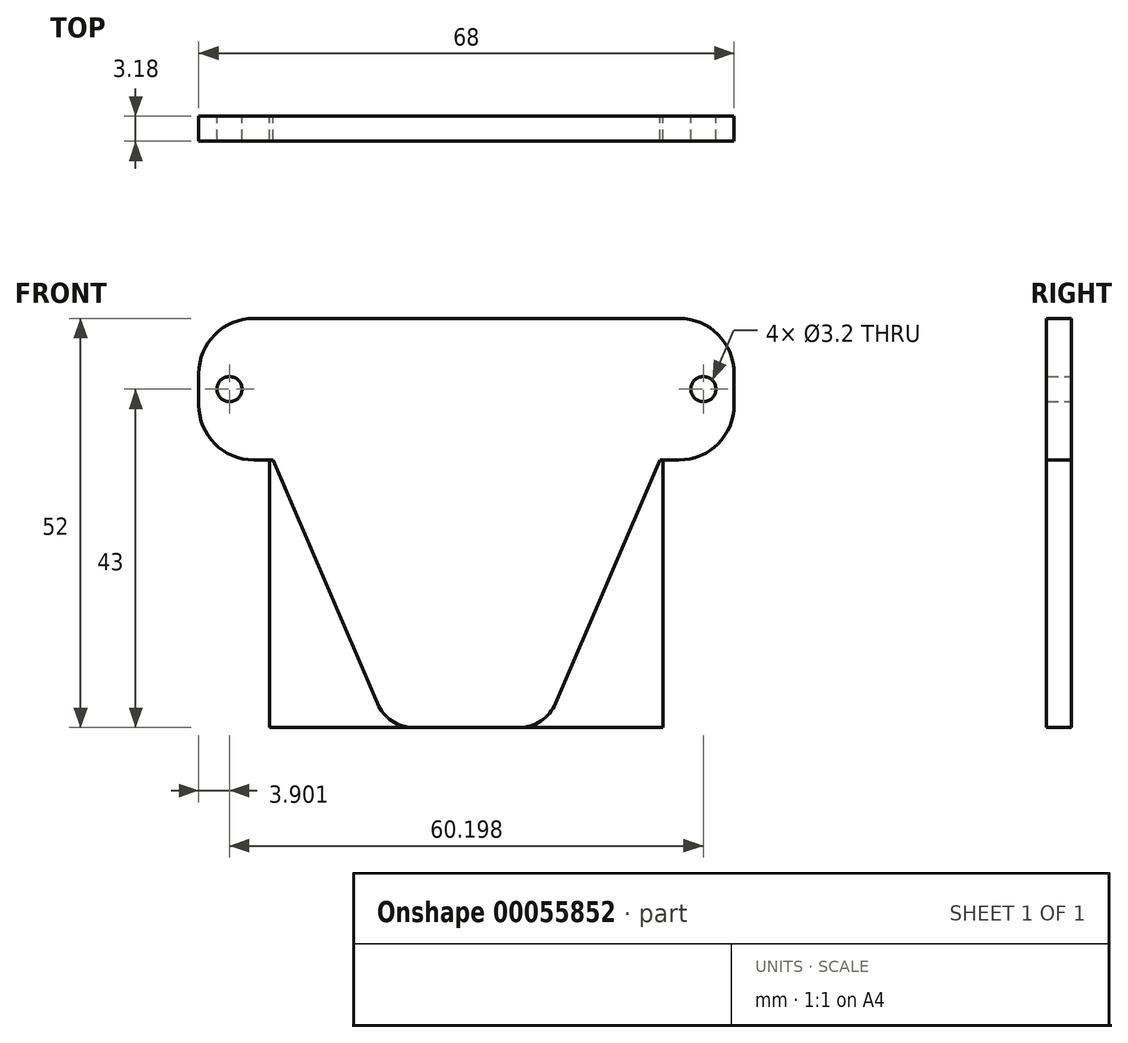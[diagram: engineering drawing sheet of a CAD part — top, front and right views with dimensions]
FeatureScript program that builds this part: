
annotation { "Feature Type Name" : "Feature", "Feature Type Description" : "" }
export const myFeature = defineFeature(function(context is Context, id is Id, definition is map)
    precondition{}
    {
        {
            var Q0;
            Q0=qCreatedBy(makeId("Front.planeOp"),FACE);
            var sketch = newSketch(context, id + "F0", { "sketchPlane" : qUnion([Q0])});
            skLineSegment(sketch, "E0.rect.top", {"start": v(-25, -21) * mm, "end": v(25, -21) * mm});
            skLineSegment(sketch, "E0.rect.left", {"start": v(-25, 13) * mm, "end": v(-25, -21) * mm});
            skLineSegment(sketch, "E0.rect.right", {"start": v(25, 13) * mm, "end": v(25, -21) * mm});
            skLineSegment(sketch, "E1.bottom", {"start": v(-25, 13) * mm, "end": v(-34, 13) * mm});
            skLineSegment(sketch, "E1.top", {"start": v(0, 31) * mm, "end": v(-34, 31) * mm});
            skLineSegment(sketch, "E1.left", {"start": v(0, 13) * mm, "end": v(0, 31) * mm});
            skLineSegment(sketch, "E1.right", {"start": v(-34, 24) * mm, "end": v(-34, 31) * mm});
            skLineSegment(sketch, "E2.bottom", {"start": v(25, 13) * mm, "end": v(34, 13) * mm});
            skLineSegment(sketch, "E2.top", {"start": v(0, 31) * mm, "end": v(34, 31) * mm});
            skLineSegment(sketch, "E2.right", {"start": v(34, 22) * mm, "end": v(34, 31) * mm});
            skCircle(sketch, "E3", {"center": v(-30.1, 22) * mm, "radius": 1.6 * mm});
            skCircle(sketch, "E4.MirrorC", {"center": v(30.1, 22) * mm, "radius": 1.6 * mm});
            skLineSegment(sketch, "E5", {"start": v(-34, 13) * mm, "end": v(-34, 24) * mm});
            skLineSegment(sketch, "E6", {"start": v(34, 13) * mm, "end": v(34, 22) * mm});
            skPoint(sketch, "E7.orphan", {"position": v(34, 13) * mm});
            skPoint(sketch, "E8.orphan", {"position": v(-34, 13) * mm});
            skSolve(sketch);
        }
        {
            var Q0;
            Q0 = qSketchRegion(id + "F0", true);
            extrude(context, id + "F1", {"entities" : qUnion([Q0]), "depth" : 3.17 * mm});
        }
        {
            var Q0;
            Q0=makeQuery(id+"F1.opExtrude","SWEPT_EDGE",EDGE,{"disambiguationData":[OSD([sQuery(id+"F0.wireOp",EDGE,"E1.top"),sQuery(id+"F0.wireOp",EDGE,"E1.right")])]});
            var Q1;
            Q1=makeQuery(id+"F1.opExtrude","SWEPT_EDGE",EDGE,{"disambiguationData":[OSD([sQuery(id+"F0.wireOp",EDGE,"E1.bottom"),sQuery(id+"F0.wireOp",EDGE,"E5")])]});
            var Q2;
            Q2=makeQuery(id+"F1.opExtrude","SWEPT_EDGE",EDGE,{"disambiguationData":[OSD([sQuery(id+"F0.wireOp",EDGE,"E2.top"),sQuery(id+"F0.wireOp",EDGE,"E2.right")])]});
            var Q3;
            Q3=makeQuery(id+"F1.opExtrude","SWEPT_EDGE",EDGE,{"disambiguationData":[OSD([sQuery(id+"F0.wireOp",EDGE,"E2.bottom"),sQuery(id+"F0.wireOp",EDGE,"E6")])]});
            fillet(context, id + "F2", {"entities" : qUnion([Q0, Q1, Q2, Q3]), "radius" : 7 * mm, "tangentPropagation" : true, "allowEdgeOverflow" : false});
        }
        {
            var Q0;
            Q0=makeQuery(id+"F1.opExtrude","SWEPT_BODY",BODY,{"disambiguationData":[OSD([sQuery(id+"F0.wireOp",EDGE,"E0.rect.top"),sQuery(id+"F0.wireOp",EDGE,"E0.rect.left"),sQuery(id+"F0.wireOp",EDGE,"E0.rect.right"),sQuery(id+"F0.wireOp",EDGE,"E1.bottom"),sQuery(id+"F0.wireOp",EDGE,"E1.top"),sQuery(id+"F0.wireOp",EDGE,"E1.right"),sQuery(id+"F0.wireOp",EDGE,"E2.bottom"),sQuery(id+"F0.wireOp",EDGE,"E2.top"),sQuery(id+"F0.wireOp",EDGE,"E2.right"),sQuery(id+"F0.wireOp",EDGE,"E3"),sQuery(id+"F0.wireOp",EDGE,"E4.MirrorC"),sQuery(id+"F0.wireOp",EDGE,"E5"),sQuery(id+"F0.wireOp",EDGE,"E6")])]});
            transform(context, id + "F3", {"entities" : qUnion([Q0]), "transformType" : TransformType.TRANSLATION_3D, "dx" : 0 * mm, "dy" : 0 * mm, "dz" : 0 * mm, "makeCopy" : true});
        }
        {
            var Q0;
            Q0=makeQuery(id+"F1.opExtrude","SWEPT_EDGE",EDGE,{"disambiguationData":[OSD([sQuery(id+"F0.wireOp",EDGE,"E0.rect.top"),sQuery(id+"F0.wireOp",EDGE,"E0.rect.left")])]});
            var Q1;
            Q1=makeQuery(id+"F1.opExtrude","SWEPT_EDGE",EDGE,{"disambiguationData":[OSD([sQuery(id+"F0.wireOp",EDGE,"E0.rect.top"),sQuery(id+"F0.wireOp",EDGE,"E0.rect.right")])]});
            chamfer(context, id + "F4", {"entities" : qUnion([Q0, Q1]), "chamferType" : ChamferType.TWO_OFFSETS, "width1" : 15 * mm, "oppositeDirection" : false, "width2" : 35 * mm, "tangentPropagation" : true});
        }
        {
            var Q0;
            {var subQ0=sQuery(id+"F0.wireOp",EDGE,"E0.rect.top");Q0=makeQuery(id+"F4.opChamfer","BLEND_EDGE",EDGE,{"blendedFrom":[makeQuery(id+"F1.opExtrude","SWEPT_EDGE",EDGE,{"disambiguationData":[OSD([subQ0,sQuery(id+"F0.wireOp",EDGE,"E0.rect.left")])]}),makeQuery(id+"F1.opExtrude","SWEPT_FACE",FACE,{"disambiguationData":[OSD([subQ0])]})],"blendedInto":[makeQuery(id+"F1.opExtrude","SWEPT_FACE",FACE,{"disambiguationData":[OSD([subQ0])]})]});}
            var Q1;
            {var subQ0=sQuery(id+"F0.wireOp",EDGE,"E0.rect.top");Q1=makeQuery(id+"F4.opChamfer","BLEND_EDGE",EDGE,{"blendedFrom":[makeQuery(id+"F1.opExtrude","SWEPT_EDGE",EDGE,{"disambiguationData":[OSD([subQ0,sQuery(id+"F0.wireOp",EDGE,"E0.rect.right")])]}),makeQuery(id+"F1.opExtrude","SWEPT_FACE",FACE,{"disambiguationData":[OSD([subQ0])]})],"blendedInto":[makeQuery(id+"F1.opExtrude","SWEPT_FACE",FACE,{"disambiguationData":[OSD([subQ0])]})]});}
            fillet(context, id + "F5", {"entities" : qUnion([Q0, Q1]), "radius" : 5.08 * mm, "tangentPropagation" : true, "allowEdgeOverflow" : false});
        }
    });
